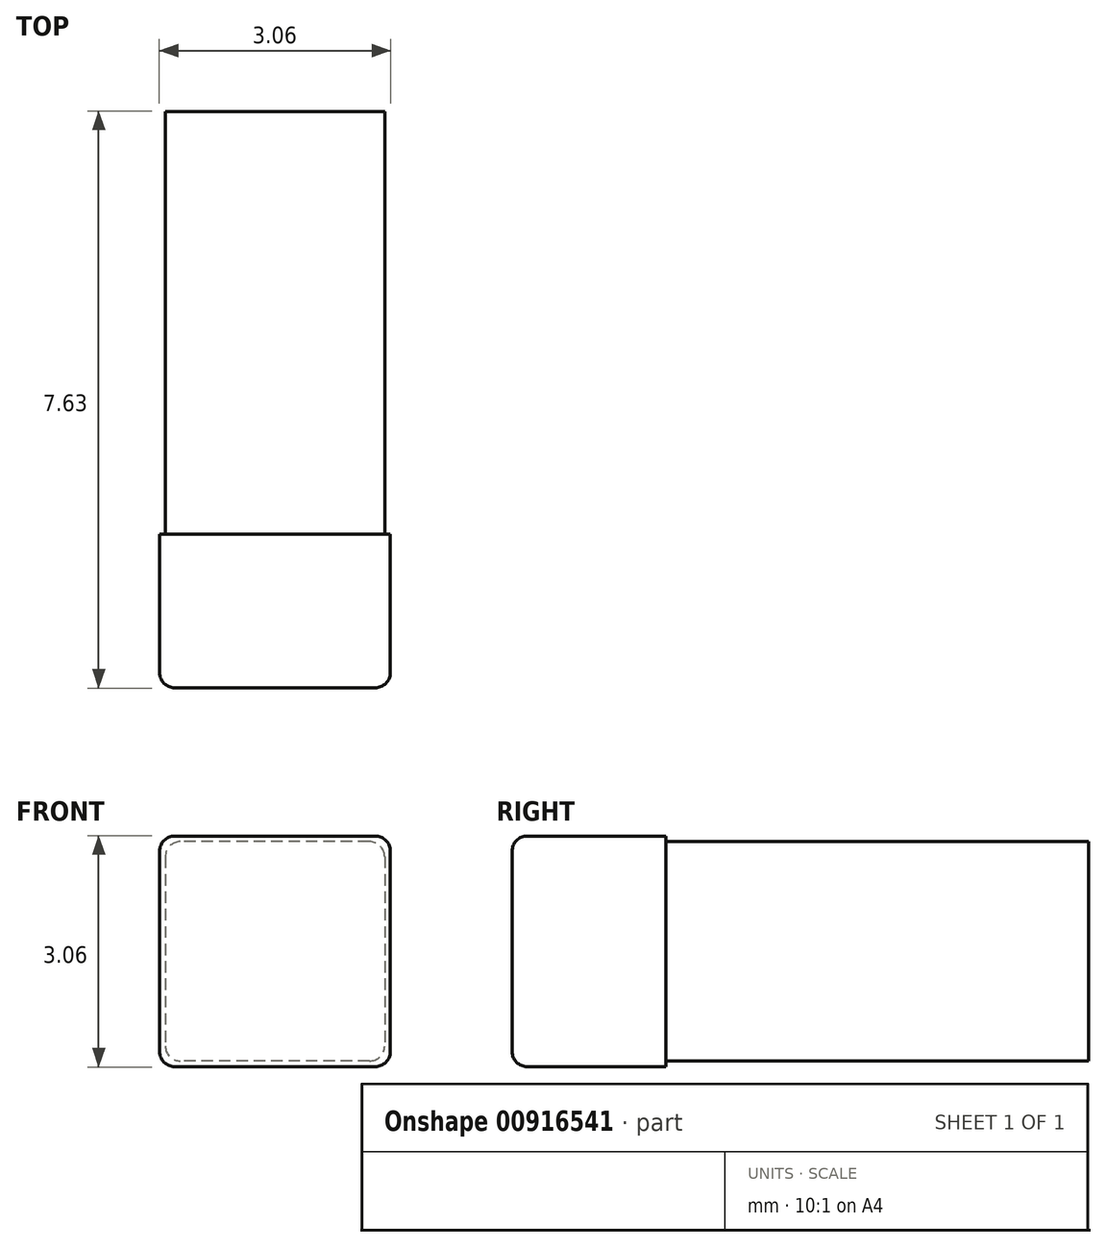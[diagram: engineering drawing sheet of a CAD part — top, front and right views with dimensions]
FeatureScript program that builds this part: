
annotation { "Feature Type Name" : "Feature", "Feature Type Description" : "" }
export const myFeature = defineFeature(function(context is Context, id is Id, definition is map)
    precondition{}
    {
        {
            assignVariable(context, id + "F0", {"name" : "CapLength", "anyValue" : 2.03});
        }
        {
            assignVariable(context, id + "F1", {"name" : "Length", "anyValue" : 9.65});
        }
        {
            var Q0;
            Q0=qCreatedBy(makeId("Front.planeOp"),FACE);
            var sketch = newSketch(context, id + "F2", { "sketchPlane" : qUnion([Q0])});
            skLineSegment(sketch, "E0.bottom", {"start": v(1.45, 1.45) * mm, "end": v(-1.45, 1.45) * mm});
            skLineSegment(sketch, "E0.top", {"start": v(1.45, -1.45) * mm, "end": v(-1.45, -1.45) * mm});
            skLineSegment(sketch, "E0.left", {"start": v(1.45, 1.45) * mm, "end": v(1.45, -1.45) * mm});
            skLineSegment(sketch, "E0.right", {"start": v(-1.45, 1.45) * mm, "end": v(-1.45, -1.45) * mm});
            skPoint(sketch, "E0.middle", {"position": v(0, 0) * mm});
            skSolve(sketch);
        }
        {
            var Q0;
            Q0=qSketchRegion(id+"F2",true);
            extrude(context, id + "F3", {"entities" : qUnion([Q0]), "depth" : (getVariable(context, 'Length') - (2 * getVariable(context, 'CapLength'))) * mm, "offsetDistance" : 25 * mm, "symmetric" : true});
        }
        {
            var Q0;
            Q0=makeQuery(id+"F3.opExtrude","CAP_FACE",FACE,{"disambiguationData":[OSD([sQuery(id+"F2.wireOp",EDGE,"E0.bottom"),sQuery(id+"F2.wireOp",EDGE,"E0.top"),sQuery(id+"F2.wireOp",EDGE,"E0.left"),sQuery(id+"F2.wireOp",EDGE,"E0.right")])],"isStart":false});
            var sketch = newSketch(context, id + "F4", { "sketchPlane" : qUnion([Q0])});
            skLineSegment(sketch, "E1.bottom", {"start": v(1.53, 1.52) * mm, "end": v(-1.52, 1.52) * mm});
            skLineSegment(sketch, "E1.top", {"start": v(1.52, -1.52) * mm, "end": v(-1.52, -1.52) * mm});
            skLineSegment(sketch, "E1.left", {"start": v(1.53, 1.52) * mm, "end": v(1.53, -1.52) * mm});
            skLineSegment(sketch, "E1.right", {"start": v(-1.52, 1.52) * mm, "end": v(-1.52, -1.52) * mm});
            skPoint(sketch, "E1.middle", {"position": v(0, 0) * mm});
            skSolve(sketch);
        }
        {
            var Q0;
            Q0=qSketchRegion(id+"F4",true);
            extrude(context, id + "F5", {"entities" : qUnion([Q0]), "depth" : (getVariable(context, 'CapLength')) * mm, "offsetDistance" : 25 * mm});
        }
        {
            var Q0;
            Q0=makeQuery(id+"F5.opExtrude","CAP_FACE",FACE,{"disambiguationData":[OSD([sQuery(id+"F4.wireOp",EDGE,"E1.bottom"),sQuery(id+"F4.wireOp",EDGE,"E1.top"),sQuery(id+"F4.wireOp",EDGE,"E1.left"),sQuery(id+"F4.wireOp",EDGE,"E1.right")])],"isStart":false});
            var Q1;
            Q1=makeQuery(id+"FsKa9ejSSYPuka9_1.1.F5.opExtrude","CAP_FACE",FACE,{"disambiguationData":[OSD([sQuery(id+"F4.wireOp",EDGE,"E1.bottom"),sQuery(id+"F4.wireOp",EDGE,"E1.top"),sQuery(id+"F4.wireOp",EDGE,"E1.left"),sQuery(id+"F4.wireOp",EDGE,"E1.right")])],"isStart":false});
            var Q2;
            Q2=makeQuery(id+"FsKa9ejSSYPuka9_1.1.F5.opExtrude","SWEPT_EDGE",EDGE,{"disambiguationData":[OSD([sQuery(id+"F4.wireOp",EDGE,"E1.bottom"),sQuery(id+"F4.wireOp",EDGE,"E1.left")])]});
            var Q3;
            Q3=makeQuery(id+"FsKa9ejSSYPuka9_1.1.F5.opExtrude","SWEPT_EDGE",EDGE,{"disambiguationData":[OSD([sQuery(id+"F4.wireOp",EDGE,"E1.top"),sQuery(id+"F4.wireOp",EDGE,"E1.left")])]});
            var Q4;
            Q4=makeQuery(id+"FsKa9ejSSYPuka9_1.1.F5.opExtrude","SWEPT_EDGE",EDGE,{"disambiguationData":[OSD([sQuery(id+"F4.wireOp",EDGE,"E1.top"),sQuery(id+"F4.wireOp",EDGE,"E1.right")])]});
            var Q5;
            Q5=makeQuery(id+"FsKa9ejSSYPuka9_1.1.F5.opExtrude","SWEPT_EDGE",EDGE,{"disambiguationData":[OSD([sQuery(id+"F4.wireOp",EDGE,"E1.bottom"),sQuery(id+"F4.wireOp",EDGE,"E1.right")])]});
            var Q6;
            Q6=makeQuery(id+"F5.opExtrude","SWEPT_EDGE",EDGE,{"disambiguationData":[OSD([sQuery(id+"F4.wireOp",EDGE,"E1.top"),sQuery(id+"F4.wireOp",EDGE,"E1.left")])]});
            var Q7;
            Q7=makeQuery(id+"F5.opExtrude","SWEPT_EDGE",EDGE,{"disambiguationData":[OSD([sQuery(id+"F4.wireOp",EDGE,"E1.top"),sQuery(id+"F4.wireOp",EDGE,"E1.right")])]});
            var Q8;
            Q8=makeQuery(id+"F5.opExtrude","SWEPT_EDGE",EDGE,{"disambiguationData":[OSD([sQuery(id+"F4.wireOp",EDGE,"E1.bottom"),sQuery(id+"F4.wireOp",EDGE,"E1.left")])]});
            var Q9;
            Q9=makeQuery(id+"F5.opExtrude","SWEPT_EDGE",EDGE,{"disambiguationData":[OSD([sQuery(id+"F4.wireOp",EDGE,"E1.bottom"),sQuery(id+"F4.wireOp",EDGE,"E1.right")])]});
            fillet(context, id + "F6", {"entities" : qUnion([Q0, Q1, Q2, Q3, Q4, Q5, Q6, Q7, Q8, Q9]), "radius" : .2 * mm, "tangentPropagation" : true, "allowEdgeOverflow" : false});
        }
        {
            var Q0;
            Q0=makeQuery(id+"F3.opExtrude","SWEPT_EDGE",EDGE,{"disambiguationData":[OSD([sQuery(id+"F2.wireOp",EDGE,"E0.bottom"),sQuery(id+"F2.wireOp",EDGE,"E0.left")])]});
            var Q1;
            Q1=makeQuery(id+"F3.opExtrude","SWEPT_EDGE",EDGE,{"disambiguationData":[OSD([sQuery(id+"F2.wireOp",EDGE,"E0.top"),sQuery(id+"F2.wireOp",EDGE,"E0.left")])]});
            var Q2;
            Q2=makeQuery(id+"F3.opExtrude","SWEPT_EDGE",EDGE,{"disambiguationData":[OSD([sQuery(id+"F2.wireOp",EDGE,"E0.bottom"),sQuery(id+"F2.wireOp",EDGE,"E0.right")])]});
            var Q3;
            Q3=makeQuery(id+"F3.opExtrude","SWEPT_EDGE",EDGE,{"disambiguationData":[OSD([sQuery(id+"F2.wireOp",EDGE,"E0.top"),sQuery(id+"F2.wireOp",EDGE,"E0.right")])]});
            fillet(context, id + "F7", {"entities" : qUnion([Q0, Q1, Q2, Q3]), "radius" : .2 * mm, "tangentPropagation" : true, "allowEdgeOverflow" : false});
        }
    });
